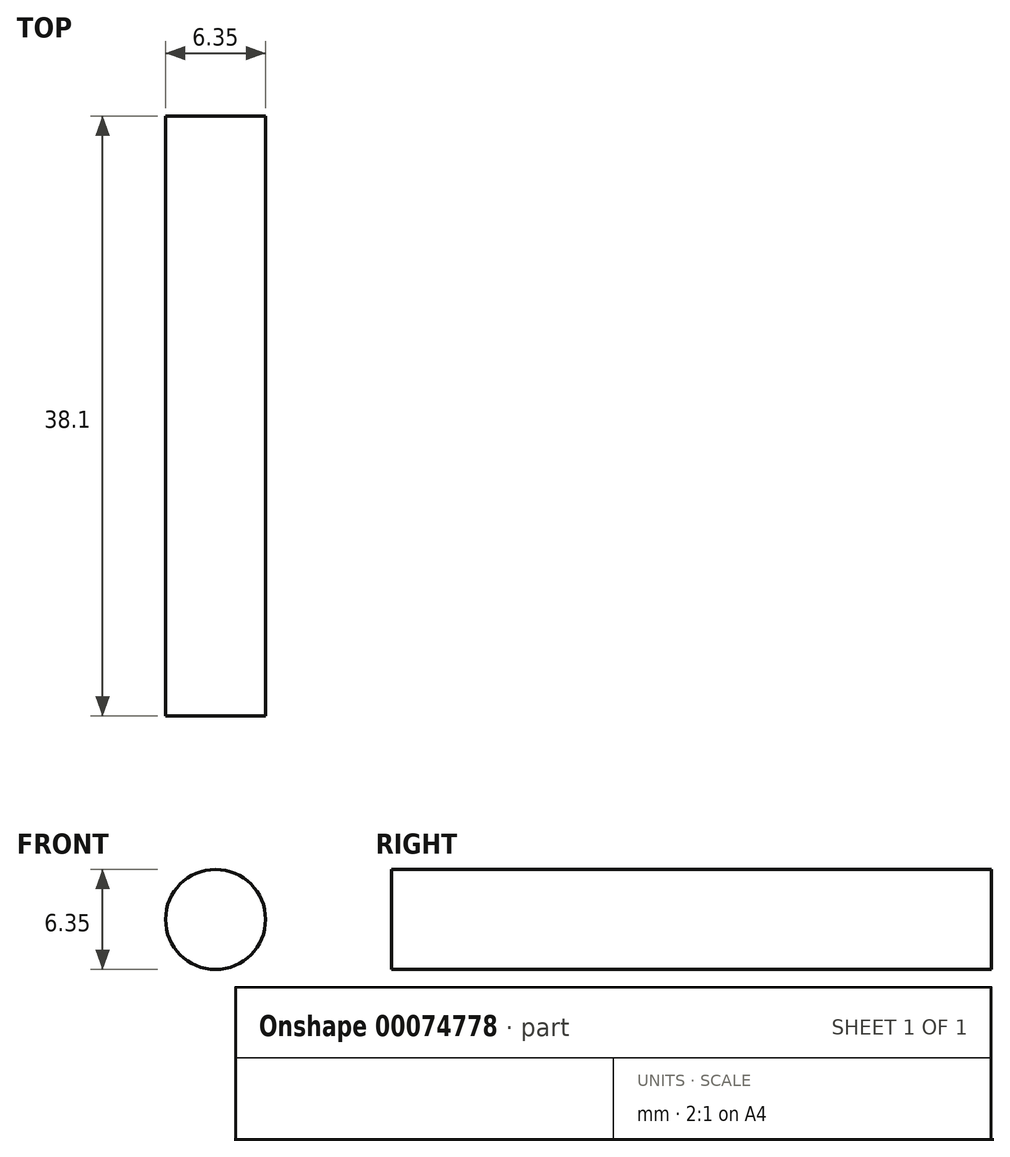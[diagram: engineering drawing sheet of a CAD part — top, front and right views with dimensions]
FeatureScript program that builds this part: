
annotation { "Feature Type Name" : "Feature", "Feature Type Description" : "" }
export const myFeature = defineFeature(function(context is Context, id is Id, definition is map)
    precondition{}
    {
        {
            var Q0;
            Q0=qCreatedBy(makeId("Front.planeOp"),FACE);
            var sketch = newSketch(context, id + "F0", { "sketchPlane" : qUnion([Q0])});
            skCircle(sketch, "E0", {"center": v(-64.15, 50.68) * mm, "radius": 3.18 * mm});
            skSolve(sketch);
        }
        {
            var Q0;
            Q0=makeQuery(id+"F0.imprint","IMPRINT",FACE,{"disambiguationData":[TD([[makeQuery(id+"F0.imprint","IMPRINT",EDGE,{"derivedFrom":sQuery(id+"F0.wireOp",EDGE,"E0")}),1.0]])]});
            extrude(context, id + "F1", {"entities" : qUnion([Q0]), "depth" : 38.1 * mm});
        }
    });
